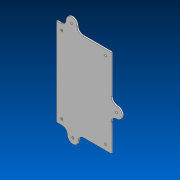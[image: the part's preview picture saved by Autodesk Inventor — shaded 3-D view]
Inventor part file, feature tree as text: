
AUTODESK INVENTOR PART (.ipt)
format: ipt  version: 2022 (Build 260153000, 153)  size: 120,832 bytes
history: native  units: in
note: dims shown in document units (in); Inventor stores cm internally (conversion verified against a paired STEP export)
features: sketch x1, extrude x1, hole x1
ambient origin geometry x8: Origin, YZ Plane, XZ Plane, XY Plane, X Axis, Y Axis, Z Axis, Center Point
bodies: Solid1 (feature_tree)
feature tree (3):
  sketch  "Sketch1"  dims[d0=4.0in d1=7.0in d2=0.5in d3=0.5in d4=0.125in d5=0.0in d6=0.18in d7=0.75in d8=0.375in d9=0.25in d10=0.5635in d11=1.0in d12=0.8108in d13=1.0in d14=5.0in d15=4.125in d16=4.0in]
  extrude  "Extrusion1"  Depth=4.0in
  hole  "Hole1"  [1 undecoded]
note: 1 required parameter value undecoded (feature->parameter linkage not recoverable at this tier; creation-order binding heuristic only, values carry confidence <= 0.55)
